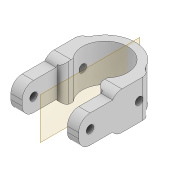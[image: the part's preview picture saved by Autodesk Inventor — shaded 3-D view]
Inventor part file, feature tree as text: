
AUTODESK INVENTOR PART (.ipt)
format: ipt  version: 2022 (Build 260153000, 153)  size: 243,200 bytes
history: native  units: mm
features: extrude x6, sketch x6, fillet x3, projected_geometry x3, mirror x1
ambient origin geometry x8: Origin, YZ Plane, XZ Plane, XY Plane, X Axis, Y Axis, Z Axis, Center Point
bodies: Solid1 (feature_tree)
feature tree (19):
  extrude  "Extrusion1"  Depth=8.0mm
  fillet  "Fillet1"  Radius=8.0mm
  extrude  "Extrusion2"  Depth=1.5mm
  extrude  "Extrusion3"  Depth=1.5mm
  fillet  "Fillet2"  Radius=2.0mm
  mirror  "Mirror1"
  extrude  "Extrusion6"  Depth=100.0mm TaperAngle=0.0deg
  extrude  "Extrusion7"  Depth=2.0mm
  extrude  "Extrusion8"  Depth=3.0mm
  fillet  "Fillet5"  Radius=3.0mm
  sketch  "Sketch1"  dims[d0=12.0mm d1=2.0mm d3=8.0mm]
  sketch  "Sketch2"  dims[d4=1.5mm d5=1.5mm]
  projected_geometry  "Projected Loop1"
  sketch  "Sketch4"  dims[d6=10.0mm d7=0.0mm d8=1.5mm d9=2.0mm]
  projected_geometry  "Projected Loop2"
  projected_geometry  "Projected Loop4"
  sketch  "Sketch7"  dims[d10=2.0mm d12=100.0mm d13=0.0mm]
  sketch  "Sketch8"  dims[d14=2.0mm d15=0.0mm d16=2.0mm]
  sketch  "Sketch9"  dims[d22=3.0mm d28=5.0mm d29=3.0mm d30=2.0mm d31=5.0mm d32=100.0mm d33=0.0mm d34=9.0mm d35=9.0mm d36=1.3mm d37=0.0mm d38=9.0mm d39=9.0mm d40=1.3mm d41=0.0mm]
